# Revit family: Gleitplatte 2x 1 1-4 Zoll
name_source: partatom
category: HLS-Bauteile
revit_build: Autodesk Revit 2017 (Build: 20190507_1515(x64)
units: mm (PartAtom-declared; Revit-internal decimal feet)

## family parameters
Arbeitsebenenbasiert = Ja
Beim Laden mit Abzugskörper schneiden = Nein
Bemaßung runder Anschluss = Durchmesser verwenden
Gemeinsam genutzt = Ja
Immer vertikal = Nein
OmniClass-Nummer = 23.75.00.00
OmniClass-Titel = Climate Control (HVAC)
Raumberechnungspunkt = Nein
Teiletyp = Normal

## types (2) — shared parameters
Abstand zur Außenkante = 35 mm  [stored 0.114829 ft]
Achsmaß = 35 mm
Anschluss = 1 1/4''
Anschlüsse = Runde Gewindeanschlusse parametrik : Muffe 1 1/4´´ (0009898)
Anzahl Anschlüsse = 2
Fabrikat = MEFA
Firma = MEFA Befestigungs- und Montagesysteme GmbH
Höhe Gewindeanschluss HGW = 20 mm  [stored 0.0656168 ft]
Kurztext2 = Anschluss 2 x 1 1/4''
Mengeneinheit = St
Stärke = 12 mm  [stored 0.0393701 ft]
vpe = 1 St
zero-valued in all types: Vorgabe-Ansicht

## per-type parameters (varying)
| type | Artikelnummer | Breite | EAN | Gewicht | Gewicht pro Bauteil | Kurztext1 | Länge | max. zul. Last |
| Gleitplatte 350x200x12, 2x 1 1/4" | 0771902 | 200 mm  [stored 0.656168 ft] | 4250928418395 | 6.93 kg | 6.93 kg | Gleitplatte 350 x 200 x 12 | 350 mm  [stored 1.14829 ft] | 6.00 kN |
| Gleitplatte 400x250x12, 2x 1 1/4" | 0771973 | 250 mm | 4250928418418 | 9.81 kg | 9.81 kg | Gleitplatte 350 x 250 x 12 | 400 mm | 5.40 kN |

note: [stored X ft] marks values corroborated as IEEE doubles in the binary element streams (Revit-internal decimal feet)

## geometry (parser evidence)
native form markers: Sweep x1
no freeform markers — native parametric forms only
